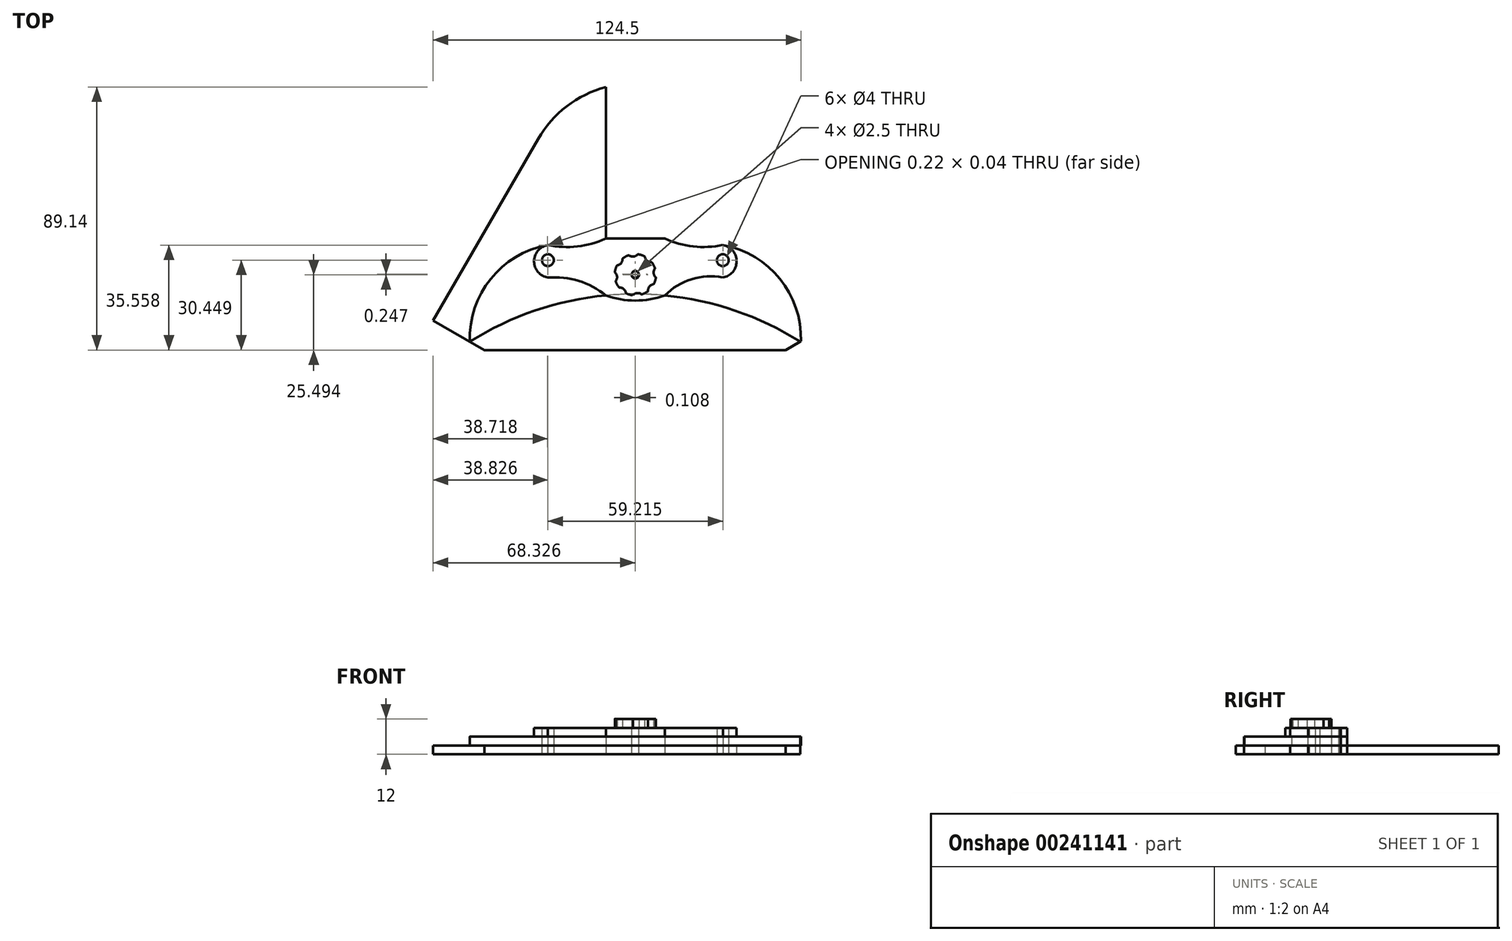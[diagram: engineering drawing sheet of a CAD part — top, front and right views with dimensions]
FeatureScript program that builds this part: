
annotation { "Feature Type Name" : "Feature", "Feature Type Description" : "" }
export const myFeature = defineFeature(function(context is Context, id is Id, definition is map)
    precondition{}
    {
        {
            var Q0;
            Q0=qCreatedBy(makeId("Top.planeOp"),FACE);
            var sketch = newSketch(context, id + "F0", { "sketchPlane" : qUnion([Q0])});
            skLineSegment(sketch, "E0.1.2", {"start": v(274.1, -221.59) * mm, "end": v(154.1, -13.74) * mm});
            skLineSegment(sketch, "E0.2.2", {"start": v(88.46, -13.74) * mm, "end": v(-31.54, -221.59) * mm});
            skArc(sketch, "E1", {"start": v(154.1, -13.74) * mm, "mid": v(121.28, 5.2) * mm, "end": v(88.46, -13.74) * mm});
            skPoint(sketch, "E2.middle.positionSnap0", {"position": v(121.28, 5.2) * mm});
            skPoint(sketch, "E2.centerSnap0", {"position": v(121.28, 5.2) * mm});
            skLineSegment(sketch, "E3", {"start": v(43.61, -79.4) * mm, "end": v(41.02, -77.9) * mm});
            skLineSegment(sketch, "E4.1.15", {"start": v(179.13, -77.1) * mm, "end": v(178.38, -75.8) * mm, "construction": true});
            skLineSegment(sketch, "E4.1.16", {"start": v(179.13, -77.1) * mm, "end": v(179.88, -78.4) * mm, "construction": true});
            skArc(sketch, "E4.2.2", {"start": v(118.32, -30.04) * mm, "mid": v(119.4, -30.46) * mm, "end": v(120.53, -30.7) * mm});
            skLineSegment(sketch, "E5", {"start": v(121.28, -54.8) * mm, "end": v(91.78, -54.8) * mm, "construction": true});
            skCircle(sketch, "E6", {"center": v(91.78, -54.8) * mm, "radius": 2 * mm});
            skLineSegment(sketch, "E7.bottom", {"start": v(111.38, 14.33) * mm, "end": v(131.38, 14.33) * mm});
            skLineSegment(sketch, "E7.left", {"start": v(111.38, 14.33) * mm, "end": v(111.38, -61.83) * mm});
            skLineSegment(sketch, "E7.right", {"start": v(131.38, 14.33) * mm, "end": v(131.38, -61.83) * mm});
            skCircle(sketch, "E8.0", {"center": v(121.27, -171.26) * mm, "radius": 105 * mm});
            skLineSegment(sketch, "E9", {"start": v(111.38, -47.44) * mm, "end": v(131.38, -47.44) * mm});
            skLineSegment(sketch, "E10", {"start": v(70.27, -85.24) * mm, "end": v(52.95, -75.24) * mm});
            skLineSegment(sketch, "E11.MirrorCS", {"start": v(172.28, -85.24) * mm, "end": v(189.6, -75.24) * mm});
            skCircle(sketch, "E12", {"center": v(121.28, -59.5) * mm, "radius": 1.25 * mm});
            skArc(sketch, "E13", {"start": v(111.38, -66.73) * mm, "mid": v(121.38, -68.47) * mm, "end": v(131.38, -66.75) * mm});
            skCircle(sketch, "E14.MirrorC", {"center": v(151, -54.8) * mm, "radius": 2 * mm});
            skArc(sketch, "E15", {"start": v(111.38, -66.73) * mm, "mid": v(102.16, -61.82) * mm, "end": v(91.78, -60.67) * mm});
            skArc(sketch, "E16", {"start": v(91.78, -49.66) * mm, "mid": v(101.76, -50.13) * mm, "end": v(111.38, -47.44) * mm});
            skArc(sketch, "E17", {"start": v(91.78, -49.66) * mm, "mid": v(87.1, -55.17) * mm, "end": v(91.78, -60.67) * mm});
            skArc(sketch, "E18.MirrorCS", {"start": v(151, -49.66) * mm, "mid": v(155.67, -55.17) * mm, "end": v(151, -60.67) * mm});
            skArc(sketch, "E19.MirrorCS", {"start": v(151, -49.66) * mm, "mid": v(141, -50.13) * mm, "end": v(131.38, -47.44) * mm});
            skLineSegment(sketch, "E20", {"start": v(70.27, -85.24) * mm, "end": v(172.28, -85.24) * mm});
            skArc(sketch, "E21", {"start": v(151, -60.67) * mm, "mid": v(140.42, -61.23) * mm, "end": v(131.38, -66.75) * mm});
            skArc(sketch, "E22", {"start": v(91.78, -49.66) * mm, "mid": v(72.46, -61.1) * mm, "end": v(65.34, -82.4) * mm});
            skArc(sketch, "E23.MirrorCS", {"start": v(151, -49.66) * mm, "mid": v(170.31, -61.1) * mm, "end": v(177.43, -82.4) * mm});
            skCircle(sketch, "E24", {"center": v(121.38, -23.75) * mm, "radius": 1.25 * mm});
            skArc(sketch, "E25", {"start": v(119.31, -17.16) * mm, "mid": v(120.79, -17.55) * mm, "end": v(122.16, -16.88) * mm});
            skArc(sketch, "E26.1.0", {"start": v(115.26, -20.55) * mm, "mid": v(116.58, -19.79) * mm, "end": v(117.08, -18.35) * mm});
            skArc(sketch, "E26.2.0", {"start": v(114.8, -25.82) * mm, "mid": v(115.2, -24.34) * mm, "end": v(114.52, -22.97) * mm});
            skArc(sketch, "E27.2.3.0", {"start": v(118.19, -29.87) * mm, "mid": v(117.43, -28.55) * mm, "end": v(115.99, -28.05) * mm});
            skArc(sketch, "E27.2.4.0", {"start": v(123.45, -30.33) * mm, "mid": v(121.92, -29.95) * mm, "end": v(120.53, -30.7) * mm});
            skArc(sketch, "E27.2.5.0", {"start": v(127.5, -26.94) * mm, "mid": v(126.19, -27.7) * mm, "end": v(125.69, -29.14) * mm});
            skArc(sketch, "E27.2.6.0", {"start": v(127.97, -21.68) * mm, "mid": v(127.58, -23.15) * mm, "end": v(128.25, -24.52) * mm});
            skArc(sketch, "E27.2.7.0", {"start": v(124.56, -17.5) * mm, "mid": v(125.3, -18.9) * mm, "end": v(126.78, -19.44) * mm});
            skArc(sketch, "E28.trimOffspring", {"start": v(123.66, -30.36) * mm, "mid": v(124.67, -29.93) * mm, "end": v(125.6, -29.34) * mm});
            skArc(sketch, "E29.trimOffspring", {"start": v(127.68, -26.81) * mm, "mid": v(128.08, -25.8) * mm, "end": v(128.32, -24.72) * mm});
            skArc(sketch, "E30.trimOffspring", {"start": v(128, -21.47) * mm, "mid": v(127.56, -20.46) * mm, "end": v(126.97, -19.53) * mm});
            skArc(sketch, "E31.trimOffspring", {"start": v(124.56, -17.5) * mm, "mid": v(123.49, -17.07) * mm, "end": v(122.36, -16.81) * mm});
            skArc(sketch, "E32.trimOffspring", {"start": v(119.1, -17.13) * mm, "mid": v(118.1, -17.57) * mm, "end": v(117.17, -18.16) * mm});
            skArc(sketch, "E33.trimOffspring", {"start": v(115.1, -20.68) * mm, "mid": v(114.69, -21.7) * mm, "end": v(114.45, -22.77) * mm});
            skArc(sketch, "E34.trimOffspring", {"start": v(114.77, -26.03) * mm, "mid": v(115.2, -27.03) * mm, "end": v(115.8, -27.96) * mm});
            skPoint(sketch, "E35.visualSharp", {"position": v(115.87, -28.06) * mm});
            skArc(sketch, "E35.filletArc", {"start": v(115.8, -27.96) * mm, "mid": v(115.88, -28.03) * mm, "end": v(115.99, -28.05) * mm});
            skPoint(sketch, "E36.visualSharp", {"position": v(114.73, -25.9) * mm});
            skArc(sketch, "E36.filletArc", {"start": v(114.8, -25.82) * mm, "mid": v(114.76, -25.92) * mm, "end": v(114.77, -26.03) * mm});
            skPoint(sketch, "E37.visualSharp", {"position": v(114.44, -22.9) * mm});
            skArc(sketch, "E37.filletArc", {"start": v(114.45, -22.77) * mm, "mid": v(114.46, -22.88) * mm, "end": v(114.52, -22.97) * mm});
            skPoint(sketch, "E38.visualSharp", {"position": v(115.15, -20.57) * mm});
            skArc(sketch, "E38.filletArc", {"start": v(115.26, -20.55) * mm, "mid": v(115.16, -20.6) * mm, "end": v(115.1, -20.68) * mm});
            skPoint(sketch, "E39.visualSharp", {"position": v(117.07, -18.23) * mm});
            skArc(sketch, "E39.filletArc", {"start": v(117.17, -18.16) * mm, "mid": v(117.1, -18.24) * mm, "end": v(117.08, -18.35) * mm});
            skPoint(sketch, "E40.visualSharp", {"position": v(119.22, -17.09) * mm});
            skArc(sketch, "E40.filletArc", {"start": v(119.31, -17.16) * mm, "mid": v(119.21, -17.12) * mm, "end": v(119.1, -17.13) * mm});
            skPoint(sketch, "E41.visualSharp", {"position": v(118.2, -29.98) * mm});
            skArc(sketch, "E41.filletArc", {"start": v(118.19, -29.87) * mm, "mid": v(118.23, -29.97) * mm, "end": v(118.32, -30.04) * mm});
            skPoint(sketch, "E42.visualSharp", {"position": v(123.55, -30.4) * mm});
            skArc(sketch, "E42.filletArc", {"start": v(123.45, -30.33) * mm, "mid": v(123.56, -30.37) * mm, "end": v(123.66, -30.36) * mm});
            skPoint(sketch, "E43.visualSharp", {"position": v(125.7, -29.26) * mm});
            skArc(sketch, "E43.filletArc", {"start": v(125.6, -29.34) * mm, "mid": v(125.67, -29.25) * mm, "end": v(125.69, -29.14) * mm});
            skPoint(sketch, "E44.visualSharp", {"position": v(127.62, -26.92) * mm});
            skArc(sketch, "E44.filletArc", {"start": v(127.5, -26.94) * mm, "mid": v(127.6, -26.9) * mm, "end": v(127.68, -26.81) * mm});
            skPoint(sketch, "E45.visualSharp", {"position": v(128.33, -24.6) * mm});
            skArc(sketch, "E45.filletArc", {"start": v(128.32, -24.72) * mm, "mid": v(128.3, -24.61) * mm, "end": v(128.25, -24.52) * mm});
            skPoint(sketch, "E46.visualSharp", {"position": v(128.04, -21.58) * mm});
            skArc(sketch, "E46.filletArc", {"start": v(127.97, -21.68) * mm, "mid": v(128.01, -21.57) * mm, "end": v(128, -21.47) * mm});
            skPoint(sketch, "E47.visualSharp", {"position": v(126.9, -19.43) * mm});
            skArc(sketch, "E47.filletArc", {"start": v(126.97, -19.53) * mm, "mid": v(126.89, -19.46) * mm, "end": v(126.78, -19.44) * mm});
            skPoint(sketch, "E48.visualSharp", {"position": v(122.23, -16.8) * mm});
            skArc(sketch, "E48.filletArc", {"start": v(122.36, -16.81) * mm, "mid": v(122.25, -16.82) * mm, "end": v(122.16, -16.88) * mm});
            skSolve(sketch);
        }
        {
            var Q0;
            Q0=makeQuery(id+"F0.imprint","IMPRINT",FACE,{"disambiguationData":[TD([[makeQuery(id+"F0.imprint","IMPRINT",EDGE,{"derivedFrom":sQuery(id+"F0.wireOp",EDGE,"E6")}),-1.0]])]});
            var Q1;
            {var subQ4=sQuery(id+"F0.wireOp",EDGE,"E13");Q1=makeQuery(id+"F0.imprint","IMPRINT",FACE,{"disambiguationData":[TD([[makeQuery(id+"F0.imprint","IMPRINT",EDGE,{"derivedFrom":subQ4}),-1.0]])]});}
            var Q2;
            {var subQ0=sQuery(id+"F0.wireOp",EDGE,"E13");Q2=makeQuery(id+"F0.imprint","IMPRINT",FACE,{"disambiguationData":[TD([[makeQuery(id+"F0.imprint","IMPRINT",EDGE,{"derivedFrom":subQ0}),1.0]])]});}
            var Q3;
            {var subQ0=sQuery(id+"F0.wireOp",EDGE,"E15");Q3=makeQuery(id+"F0.imprint","IMPRINT",FACE,{"disambiguationData":[TD([[makeQuery(id+"F0.imprint","IMPRINT",EDGE,{"derivedFrom":subQ0}),1.0]])]});}
            var Q4;
            Q4=makeQuery(id+"F0.imprint","IMPRINT",FACE,{"disambiguationData":[TD([[makeQuery(id+"F0.imprint","IMPRINT",EDGE,{"derivedFrom":sQuery(id+"F0.wireOp",EDGE,"E18.MirrorCS")}),1.0]])]});
            var Q5;
            {var subQ5=sQuery(id+"F0.wireOp",EDGE,"E16");Q5=makeQuery(id+"F0.imprint","IMPRINT",FACE,{"disambiguationData":[TD([[makeQuery(id+"F0.imprint","IMPRINT",EDGE,{"derivedFrom":subQ5}),1.0]])]});}
            var Q6;
            {var subQ5=sQuery(id+"F0.wireOp",EDGE,"E19.MirrorCS");Q6=makeQuery(id+"F0.imprint","IMPRINT",FACE,{"disambiguationData":[TD([[makeQuery(id+"F0.imprint","IMPRINT",EDGE,{"derivedFrom":subQ5}),-1.0]])]});}
            var Q7;
            Q7=makeQuery(id+"F0.imprint","IMPRINT",FACE,{"disambiguationData":[TD([[makeQuery(id+"F0.imprint","IMPRINT",EDGE,{"derivedFrom":sQuery(id+"F0.wireOp",EDGE,"E4.2.2")}),1.0]])]});
            extrude(context, id + "F1", {"entities" : qUnion([Q0, Q1, Q2, Q3, Q4, Q5, Q6, Q7]), "depth" : 3 * mm, "offsetDistance" : 25 * mm});
        }
        {
            var Q0;
            Q0=makeQuery(id+"F0.imprint","IMPRINT",FACE,{"disambiguationData":[TD([[makeQuery(id+"F0.imprint","IMPRINT",EDGE,{"derivedFrom":sQuery(id+"F0.wireOp",EDGE,"E6")}),-1.0]])]});
            var Q1;
            {var subQ0=sQuery(id+"F0.wireOp",EDGE,"E13");Q1=makeQuery(id+"F0.imprint","IMPRINT",FACE,{"disambiguationData":[TD([[makeQuery(id+"F0.imprint","IMPRINT",EDGE,{"derivedFrom":subQ0}),1.0]])]});}
            extrude(context, id + "F2", {"entities" : qUnion([Q0, Q1]), "depth" : 3 * mm, "offsetDistance" : 25 * mm});
        }
        {
            var Q0;
            Q0=makeQuery(id+"F0.imprint","IMPRINT",FACE,{"disambiguationData":[TD([[makeQuery(id+"F0.imprint","IMPRINT",EDGE,{"derivedFrom":sQuery(id+"F0.wireOp",EDGE,"E6")}),-1.0]])]});
            var Q1;
            {var subQ0=sQuery(id+"F0.wireOp",EDGE,"E21");Q1=makeQuery(id+"F0.imprint","IMPRINT",FACE,{"disambiguationData":[TD([[makeQuery(id+"F0.imprint","IMPRINT",EDGE,{"derivedFrom":subQ0}),1.0]])]});}
            var Q2;
            {var subQ0=sQuery(id+"F0.wireOp",EDGE,"E15");Q2=makeQuery(id+"F0.imprint","IMPRINT",FACE,{"disambiguationData":[TD([[makeQuery(id+"F0.imprint","IMPRINT",EDGE,{"derivedFrom":subQ0}),1.0]])]});}
            extrude(context, id + "F3", {"entities" : qUnion([Q0, Q1, Q2]), "depth" : 3 * mm, "offsetDistance" : 25 * mm});
        }
        {
            var Q0;
            Q0=makeQuery(id+"F3.opExtrude","SWEPT_BODY",BODY,{"disambiguationData":[OSD([sQuery(id+"F0.wireOp",EDGE,"E6"),sQuery(id+"F0.wireOp",EDGE,"E8.0"),sQuery(id+"F0.wireOp",EDGE,"E9"),sQuery(id+"F0.wireOp",EDGE,"E12"),sQuery(id+"F0.wireOp",EDGE,"E14.MirrorC"),sQuery(id+"F0.wireOp",EDGE,"E15"),sQuery(id+"F0.wireOp",EDGE,"E16"),sQuery(id+"F0.wireOp",EDGE,"E17"),sQuery(id+"F0.wireOp",EDGE,"E18.MirrorCS"),sQuery(id+"F0.wireOp",EDGE,"E19.MirrorCS"),sQuery(id+"F0.wireOp",EDGE,"E21")])]});
            transform(context, id + "F4", {"entities" : qUnion([Q0]), "transformType" : TransformType.TRANSLATION_3D, "dx" : 0 * mm, "dy" : 0 * mm, "dz" : 3 * mm, "makeCopy" : false});
        }
        {
            var Q0;
            Q0=makeQuery(id+"F2.opExtrude","SWEPT_BODY",BODY,{"disambiguationData":[OSD([sQuery(id+"F0.wireOp",EDGE,"E6"),sQuery(id+"F0.wireOp",EDGE,"E9"),sQuery(id+"F0.wireOp",EDGE,"E12"),sQuery(id+"F0.wireOp",EDGE,"E13"),sQuery(id+"F0.wireOp",EDGE,"E14.MirrorC"),sQuery(id+"F0.wireOp",EDGE,"E15"),sQuery(id+"F0.wireOp",EDGE,"E16"),sQuery(id+"F0.wireOp",EDGE,"E17"),sQuery(id+"F0.wireOp",EDGE,"E18.MirrorCS"),sQuery(id+"F0.wireOp",EDGE,"E19.MirrorCS"),sQuery(id+"F0.wireOp",EDGE,"E21")])]});
            transform(context, id + "F5", {"entities" : qUnion([Q0]), "transformType" : TransformType.TRANSLATION_3D, "dx" : 0 * mm, "dy" : 0 * mm, "dz" : 6 * mm, "makeCopy" : false});
        }
        {
            var Q0;
            Q0=makeQuery(id+"F1.opExtrude","SWEPT_BODY",BODY,{"disambiguationData":[OSD([sQuery(id+"F0.wireOp",EDGE,"E4.2.2"),sQuery(id+"F0.wireOp",EDGE,"E24"),sQuery(id+"F0.wireOp",EDGE,"E25"),sQuery(id+"F0.wireOp",EDGE,"E26.1.0"),sQuery(id+"F0.wireOp",EDGE,"E26.2.0"),sQuery(id+"F0.wireOp",EDGE,"E27.2.3.0"),sQuery(id+"F0.wireOp",EDGE,"E27.2.4.0"),sQuery(id+"F0.wireOp",EDGE,"E27.2.5.0"),sQuery(id+"F0.wireOp",EDGE,"E27.2.6.0"),sQuery(id+"F0.wireOp",EDGE,"E27.2.7.0"),sQuery(id+"F0.wireOp",EDGE,"E28.trimOffspring"),sQuery(id+"F0.wireOp",EDGE,"E29.trimOffspring"),sQuery(id+"F0.wireOp",EDGE,"E30.trimOffspring"),sQuery(id+"F0.wireOp",EDGE,"E31.trimOffspring"),sQuery(id+"F0.wireOp",EDGE,"E32.trimOffspring"),sQuery(id+"F0.wireOp",EDGE,"E33.trimOffspring"),sQuery(id+"F0.wireOp",EDGE,"E34.trimOffspring"),sQuery(id+"F0.wireOp",EDGE,"E35.filletArc"),sQuery(id+"F0.wireOp",EDGE,"E36.filletArc"),sQuery(id+"F0.wireOp",EDGE,"E37.filletArc"),sQuery(id+"F0.wireOp",EDGE,"E38.filletArc"),sQuery(id+"F0.wireOp",EDGE,"E39.filletArc"),sQuery(id+"F0.wireOp",EDGE,"E40.filletArc"),sQuery(id+"F0.wireOp",EDGE,"E41.filletArc"),sQuery(id+"F0.wireOp",EDGE,"E42.filletArc"),sQuery(id+"F0.wireOp",EDGE,"E43.filletArc"),sQuery(id+"F0.wireOp",EDGE,"E44.filletArc"),sQuery(id+"F0.wireOp",EDGE,"E45.filletArc"),sQuery(id+"F0.wireOp",EDGE,"E46.filletArc"),sQuery(id+"F0.wireOp",EDGE,"E47.filletArc"),sQuery(id+"F0.wireOp",EDGE,"E48.filletArc")])]});
            transform(context, id + "F6", {"entities" : qUnion([Q0]), "transformType" : TransformType.TRANSLATION_3D, "dx" : 0 * mm, "dy" : -36 * mm, "dz" : 9 * mm, "makeCopy" : false});
        }
    });
